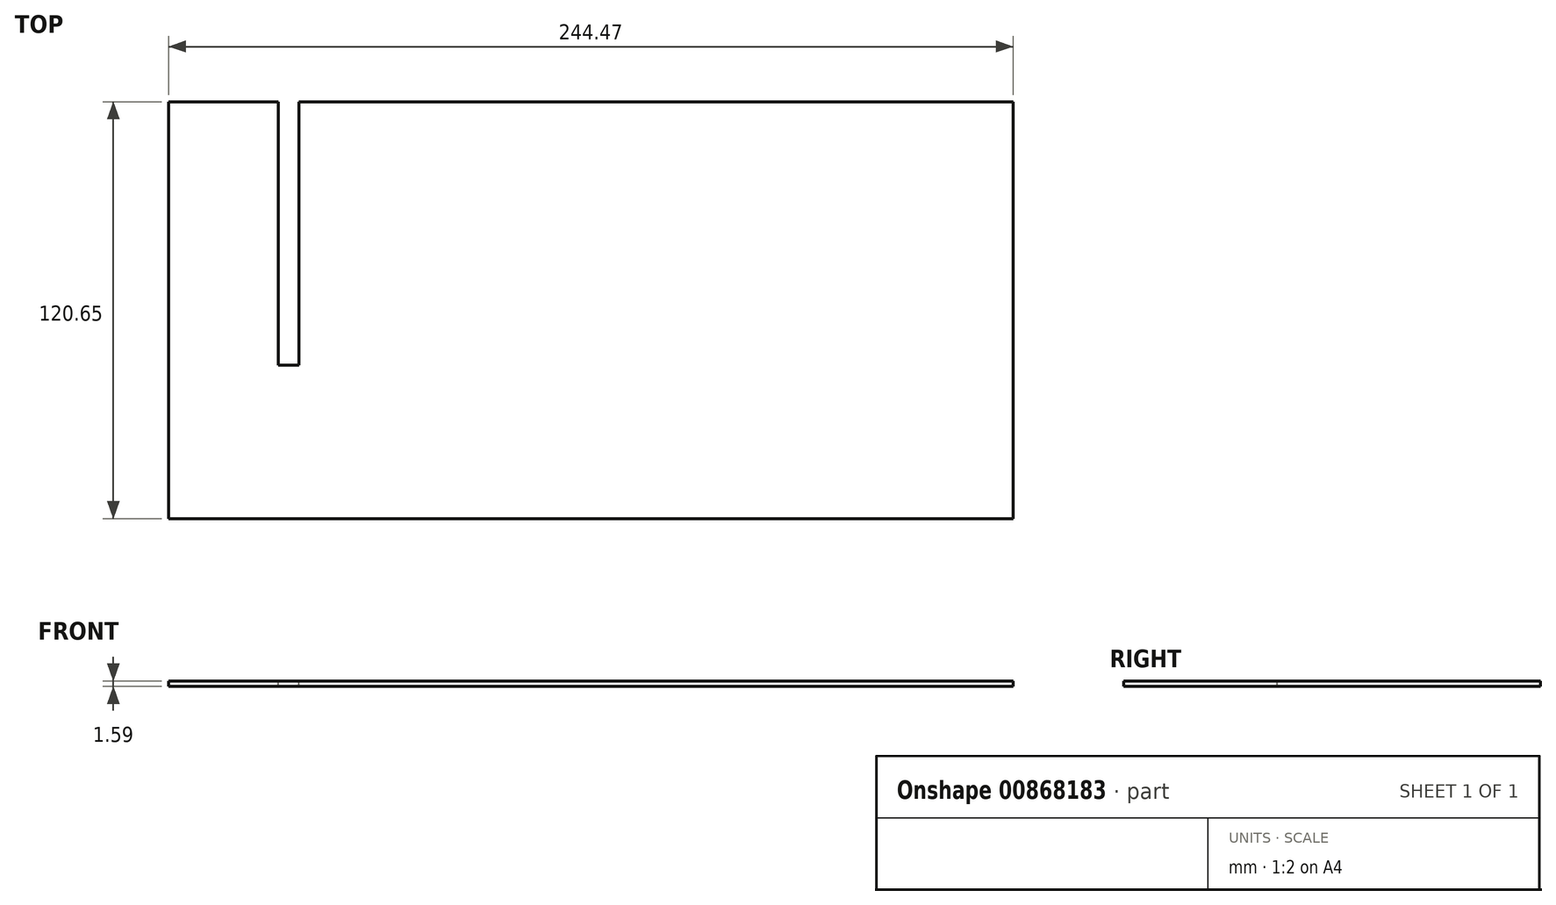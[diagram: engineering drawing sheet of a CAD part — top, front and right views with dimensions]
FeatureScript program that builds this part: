
annotation { "Feature Type Name" : "Feature", "Feature Type Description" : "" }
export const myFeature = defineFeature(function(context is Context, id is Id, definition is map)
    precondition{}
    {
        {
            var Q0;
            Q0=qCreatedBy(makeId("Top.planeOp"),FACE);
            var sketch = newSketch(context, id + "F0", { "sketchPlane" : qUnion([Q0])});
            skLineSegment(sketch, "E0.bottom", {"start": v(0, 0) * mm, "end": v(244.48, 0) * mm});
            skLineSegment(sketch, "E0.top", {"start": v(0, 120.65) * mm, "end": v(244.48, 120.65) * mm});
            skLineSegment(sketch, "E0.left", {"start": v(0, 0) * mm, "end": v(0, 120.65) * mm});
            skLineSegment(sketch, "E0.right", {"start": v(244.48, 0) * mm, "end": v(244.48, 120.65) * mm});
            skSolve(sketch);
        }
        {
            var Q0;
            Q0=makeQuery(id+"F0.imprint","IMPRINT",FACE,{"disambiguationData":[TD([[makeQuery(id+"F0.imprint","IMPRINT",EDGE,{"derivedFrom":sQuery(id+"F0.wireOp",EDGE,"E0.bottom")}),1.0]])]});
            extrude(context, id + "F1", {"entities" : qUnion([Q0]), "depth" : 1.59 * mm, "offsetDistance" : 25.4 * mm});
        }
        {
            var Q0;
            Q0=makeQuery(id+"F1.opExtrude","CAP_FACE",FACE,{"disambiguationData":[OSD([sQuery(id+"F0.wireOp",EDGE,"E0.bottom"),sQuery(id+"F0.wireOp",EDGE,"E0.top"),sQuery(id+"F0.wireOp",EDGE,"E0.left"),sQuery(id+"F0.wireOp",EDGE,"E0.right")])],"isStart":false});
            var sketch = newSketch(context, id + "F2", { "sketchPlane" : qUnion([Q0])});
            skLineSegment(sketch, "E1.bottom", {"start": v(31.75, 120.65) * mm, "end": v(37.7, 120.65) * mm});
            skLineSegment(sketch, "E2.top", {"start": v(31.75, 44.45) * mm, "end": v(37.7, 44.45) * mm});
            skLineSegment(sketch, "E2.left", {"start": v(31.75, 120.65) * mm, "end": v(31.75, 44.45) * mm});
            skLineSegment(sketch, "E2.right", {"start": v(37.7, 120.65) * mm, "end": v(37.7, 44.45) * mm});
            skSolve(sketch);
        }
        {
            var Q0;
            Q0=makeQuery(id+"F2.imprint","IMPRINT",FACE,{"disambiguationData":[TD([[makeQuery(id+"F2.imprint","IMPRINT",EDGE,{"derivedFrom":sQuery(id+"F2.wireOp",EDGE,"E1.bottom")}),-1.0]])]});
            var Q1;
            Q1=makeQuery(id+"F2.imprint","IMPRINT",FACE,{"disambiguationData":[TD([[makeQuery(id+"F2.imprint","IMPRINT",EDGE,{"derivedFrom":sQuery(id+"F2.wireOp",EDGE,"E1.bottom")}),-1.0]])]});
            extrude(context, id + "F3", {"entities" : qUnion([Q0, Q1]), "operationType" : NewBodyOperationType.REMOVE, "oppositeDirection" : true, "depth" : 25.4 * mm, "offsetDistance" : 25.4 * mm});
        }
    });
